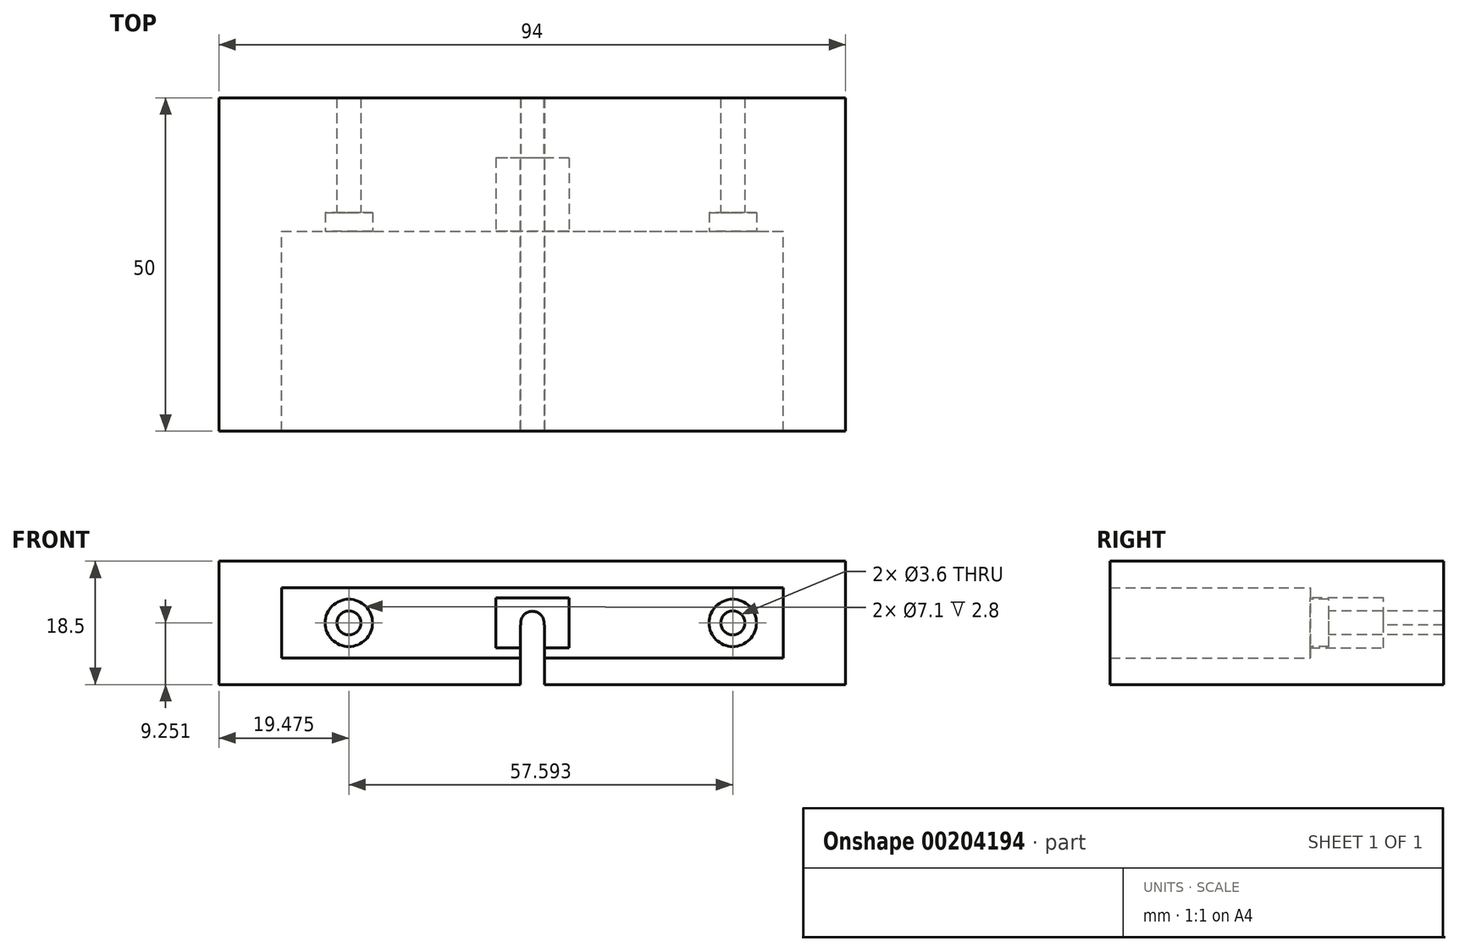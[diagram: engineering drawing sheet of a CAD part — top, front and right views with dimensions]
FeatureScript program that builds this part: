
annotation { "Feature Type Name" : "Feature", "Feature Type Description" : "" }
export const myFeature = defineFeature(function(context is Context, id is Id, definition is map)
    precondition{}
    {
        {
            var Q0;
            Q0=qCreatedBy(makeId("Front.planeOp"),FACE);
            var sketch = newSketch(context, id + "F0", { "sketchPlane" : qUnion([Q0])});
            skLineSegment(sketch, "E0.bottom", {"start": v(-39.43, 27.3) * mm, "end": v(35.82, 27.3) * mm});
            skLineSegment(sketch, "E0.top", {"start": v(-39.43, 16.8) * mm, "end": v(35.82, 16.8) * mm});
            skLineSegment(sketch, "E0.left", {"start": v(-39.43, 27.3) * mm, "end": v(-39.43, 16.8) * mm});
            skLineSegment(sketch, "E0.right", {"start": v(35.82, 27.3) * mm, "end": v(35.82, 16.8) * mm});
            skPoint(sketch, "E1", {"position": v(-1.8, 27.3) * mm});
            skPoint(sketch, "E2", {"position": v(-1.8, 16.8) * mm});
            skPoint(sketch, "E3", {"position": v(-1.8, 22.04) * mm});
            skLineSegment(sketch, "E4.bottom", {"start": v(45.2, 12.8) * mm, "end": v(-48.8, 12.8) * mm});
            skLineSegment(sketch, "E4.top", {"start": v(45.2, 31.3) * mm, "end": v(-48.8, 31.3) * mm});
            skLineSegment(sketch, "E4.left", {"start": v(45.2, 12.8) * mm, "end": v(45.2, 31.3) * mm});
            skLineSegment(sketch, "E4.right", {"start": v(-48.8, 12.8) * mm, "end": v(-48.8, 31.3) * mm});
            skPoint(sketch, "E5.orphan", {"position": v(-39.43, 22.04) * mm});
            skPoint(sketch, "E6.end.orphan", {"position": v(35.82, 22.04) * mm});
            skLineSegment(sketch, "E7.bottom", {"start": v(3.7, 18.3) * mm, "end": v(-7.3, 18.3) * mm});
            skLineSegment(sketch, "E7.top", {"start": v(3.7, 25.8) * mm, "end": v(-7.3, 25.8) * mm});
            skLineSegment(sketch, "E7.left", {"start": v(3.7, 18.3) * mm, "end": v(3.7, 25.8) * mm});
            skLineSegment(sketch, "E7.right", {"start": v(-7.3, 18.3) * mm, "end": v(-7.3, 25.8) * mm});
            skSolve(sketch);
        }
        {
            var Q0;
            Q0=makeQuery(id+"F0.imprint","IMPRINT",FACE,{"disambiguationData":[TD([[makeQuery(id+"F0.imprint","IMPRINT",EDGE,{"derivedFrom":sQuery(id+"F0.wireOp",EDGE,"E0.bottom")}),1.0]])]});
            var sketch = newSketch(context, id + "F1", { "sketchPlane" : qUnion([Q0])});
            skSolve(sketch);
        }
        {
            var Q0;
            Q0=makeQuery(id+"F0.imprint","IMPRINT",FACE,{"disambiguationData":[TD([[makeQuery(id+"F0.imprint","IMPRINT",EDGE,{"derivedFrom":sQuery(id+"F0.wireOp",EDGE,"E0.bottom")}),1.0]])]});
            extrude(context, id + "F2", {"entities" : qUnion([Q0]), "depth" : 50 * mm});
        }
        {
            var Q0;
            Q0=makeQuery(id+"F1.imprint","IMPRINT",FACE,{"disambiguationData":[TD([[makeQuery(id+"F1.imprint","IMPRINT",EDGE,{"derivedFrom":makeQuery(id+"F0.imprint","IMPRINT",EDGE,{"derivedFrom":sQuery(id+"F0.wireOp",EDGE,"E0.bottom")})}),-1.0]])]});
            extrude(context, id + "F3", {"entities" : qUnion([Q0]), "operationType" : NewBodyOperationType.ADD, "depth" : 20 * mm});
        }
        {
            var Q0;
            Q0=makeQuery(id+"F3.opExtrude","CAP_FACE",FACE,{"disambiguationData":[OSD([sQuery(id+"F0.wireOp",EDGE,"E0.bottom"),sQuery(id+"F0.wireOp",EDGE,"E0.top"),sQuery(id+"F0.wireOp",EDGE,"E0.left"),sQuery(id+"F0.wireOp",EDGE,"E0.right")])],"isStart":false});
            var sketch = newSketch(context, id + "F4", { "sketchPlane" : qUnion([Q0])});
            skPoint(sketch, "E8", {"position": v(-1.8, 22.04) * mm});
            skLineSegment(sketch, "E9.bottom", {"start": v(3.7, 18.3) * mm, "end": v(-7.3, 18.3) * mm});
            skLineSegment(sketch, "E9.top", {"start": v(3.7, 25.8) * mm, "end": v(-7.3, 25.8) * mm});
            skLineSegment(sketch, "E9.left", {"start": v(3.7, 18.3) * mm, "end": v(3.7, 25.8) * mm});
            skLineSegment(sketch, "E9.right", {"start": v(-7.3, 18.3) * mm, "end": v(-7.3, 25.8) * mm});
            skPoint(sketch, "E10.orphan", {"position": v(-1.8, 16.8) * mm});
            skPoint(sketch, "E11.start.orphan", {"position": v(-1.8, 27.3) * mm});
            skPoint(sketch, "E12.trimOffspring.end.orphan", {"position": v(-39.43, 22.04) * mm});
            skPoint(sketch, "E13.start.orphan", {"position": v(35.82, 22.04) * mm});
            skCircle(sketch, "E14", {"center": v(-1.8, 22.04) * mm, "radius": 1.75 * mm});
            skCircle(sketch, "E15", {"center": v(-29.33, 22.04) * mm, "radius": 1.8 * mm});
            skCircle(sketch, "E16", {"center": v(-29.33, 22.04) * mm, "radius": 3.55 * mm});
            skCircle(sketch, "E17", {"center": v(28.26, 22.04) * mm, "radius": 1.8 * mm});
            skCircle(sketch, "E18", {"center": v(28.26, 22.04) * mm, "radius": 3.55 * mm});
            skSolve(sketch);
        }
        {
            var Q0;
            Q0=makeQuery(id+"F4.imprint","IMPRINT",FACE,{"disambiguationData":[TD([[makeQuery(id+"F4.imprint","IMPRINT",EDGE,{"derivedFrom":sQuery(id+"F4.wireOp",EDGE,"E9.bottom")}),-1.0]])]});
            extrude(context, id + "F5", {"entities" : qUnion([Q0]), "operationType" : NewBodyOperationType.REMOVE, "oppositeDirection" : true, "depth" : 11 * mm});
        }
        {
            var Q0;
            Q0=makeQuery(id+"F5.boolean.opBoolean","SPLIT",FACE,{"disambiguationData":[TD([makeQuery(id+"F5.opExtrude","SWEPT_FACE",FACE,{"disambiguationData":[OSD([sQuery(id+"F4.wireOp",EDGE,"E14")])]})])],"derivedFrom":makeQuery(id+"F3.opExtrude","CAP_FACE",FACE,{"disambiguationData":[OSD([sQuery(id+"F0.wireOp",EDGE,"E0.bottom"),sQuery(id+"F0.wireOp",EDGE,"E0.top"),sQuery(id+"F0.wireOp",EDGE,"E0.left"),sQuery(id+"F0.wireOp",EDGE,"E0.right")])],"isStart":false})});
            extrude(context, id + "F6", {"entities" : qUnion([Q0]), "operationType" : NewBodyOperationType.REMOVE, "oppositeDirection" : true, "depth" : 27.18 * mm});
        }
        {
            var Q0;
            Q0=makeQuery(id+"F2.opExtrude","SWEPT_FACE",FACE,{"disambiguationData":[OSD([sQuery(id+"F0.wireOp",EDGE,"E4.bottom")])]});
            var sketch = newSketch(context, id + "F7", { "sketchPlane" : qUnion([Q0])});
            skLineSegment(sketch, "E19", {"start": v(-48.8, 25) * mm, "end": v(-3.6, 25) * mm});
            skLineSegment(sketch, "E20", {"start": v(-1.8, 70) * mm, "end": v(-1.8, 50) * mm});
            skLineSegment(sketch, "E21.bottom", {"start": v(-3.6, -70) * mm, "end": v(0, -70) * mm});
            skLineSegment(sketch, "E21.top", {"start": v(-3.6, 70) * mm, "end": v(0, 70) * mm});
            skLineSegment(sketch, "E21.left", {"start": v(-3.6, -70) * mm, "end": v(-3.6, 70) * mm});
            skLineSegment(sketch, "E21.right", {"start": v(0, -70) * mm, "end": v(0, 70) * mm});
            skPoint(sketch, "E21.middle", {"position": v(-1.8, 0) * mm});
            skLineSegment(sketch, "E22.trimOffspring", {"start": v(0, 25) * mm, "end": v(45.2, 25) * mm});
            skSolve(sketch);
        }
        {
            var Q0;
            {var subQ7=sQuery(id+"F7.wireOp",EDGE,"E21.left");var subQ8=makeQuery(id+"F7.imprint","INTERSECT",VERTEX,{"derivedFrom":[sQuery(id+"F7.wireOp",EDGE,"E19"),subQ7]});Q0=makeQuery(id+"F7.imprint","IMPRINT",FACE,{"disambiguationData":[TD([[makeQuery(id+"F7.imprint","IMPRINT",EDGE,{"disambiguationData":[TD([[subQ8,1.0]])],"derivedFrom":subQ7}),-1.0]])]});}
            var Q1;
            Q1=sQuery(id+"F7.wireOp",EDGE,"E21.left");
            extrude(context, id + "F8", {"entities" : qUnion([Q0]), "operationType" : NewBodyOperationType.REMOVE, "surfaceEntities" : qUnion([Q1]), "oppositeDirection" : true, "depth" : 8.94 * mm});
        }
        {
            var Q0;
            Q0=makeQuery(id+"F4.imprint","IMPRINT",FACE,{"disambiguationData":[TD([[makeQuery(id+"F4.imprint","IMPRINT",EDGE,{"derivedFrom":sQuery(id+"F4.wireOp",EDGE,"E15")}),1.0]])]});
            var Q1;
            Q1=makeQuery(id+"F4.imprint","IMPRINT",FACE,{"disambiguationData":[TD([[makeQuery(id+"F4.imprint","IMPRINT",EDGE,{"derivedFrom":sQuery(id+"F4.wireOp",EDGE,"E17")}),1.0]])]});
            extrude(context, id + "F9", {"entities" : qUnion([Q0, Q1]), "operationType" : NewBodyOperationType.REMOVE, "oppositeDirection" : true, "depth" : 25 * mm});
        }
        {
            var Q0;
            Q0=makeQuery(id+"F4.imprint","IMPRINT",FACE,{"disambiguationData":[TD([[makeQuery(id+"F4.imprint","IMPRINT",EDGE,{"derivedFrom":sQuery(id+"F4.wireOp",EDGE,"E17")}),-1.0]])]});
            var Q1;
            Q1=makeQuery(id+"F4.imprint","IMPRINT",FACE,{"disambiguationData":[TD([[makeQuery(id+"F4.imprint","IMPRINT",EDGE,{"derivedFrom":sQuery(id+"F4.wireOp",EDGE,"E15")}),-1.0]])]});
            extrude(context, id + "F10", {"entities" : qUnion([Q0, Q1]), "operationType" : NewBodyOperationType.REMOVE, "oppositeDirection" : true, "depth" : 2.8 * mm});
        }
    });
